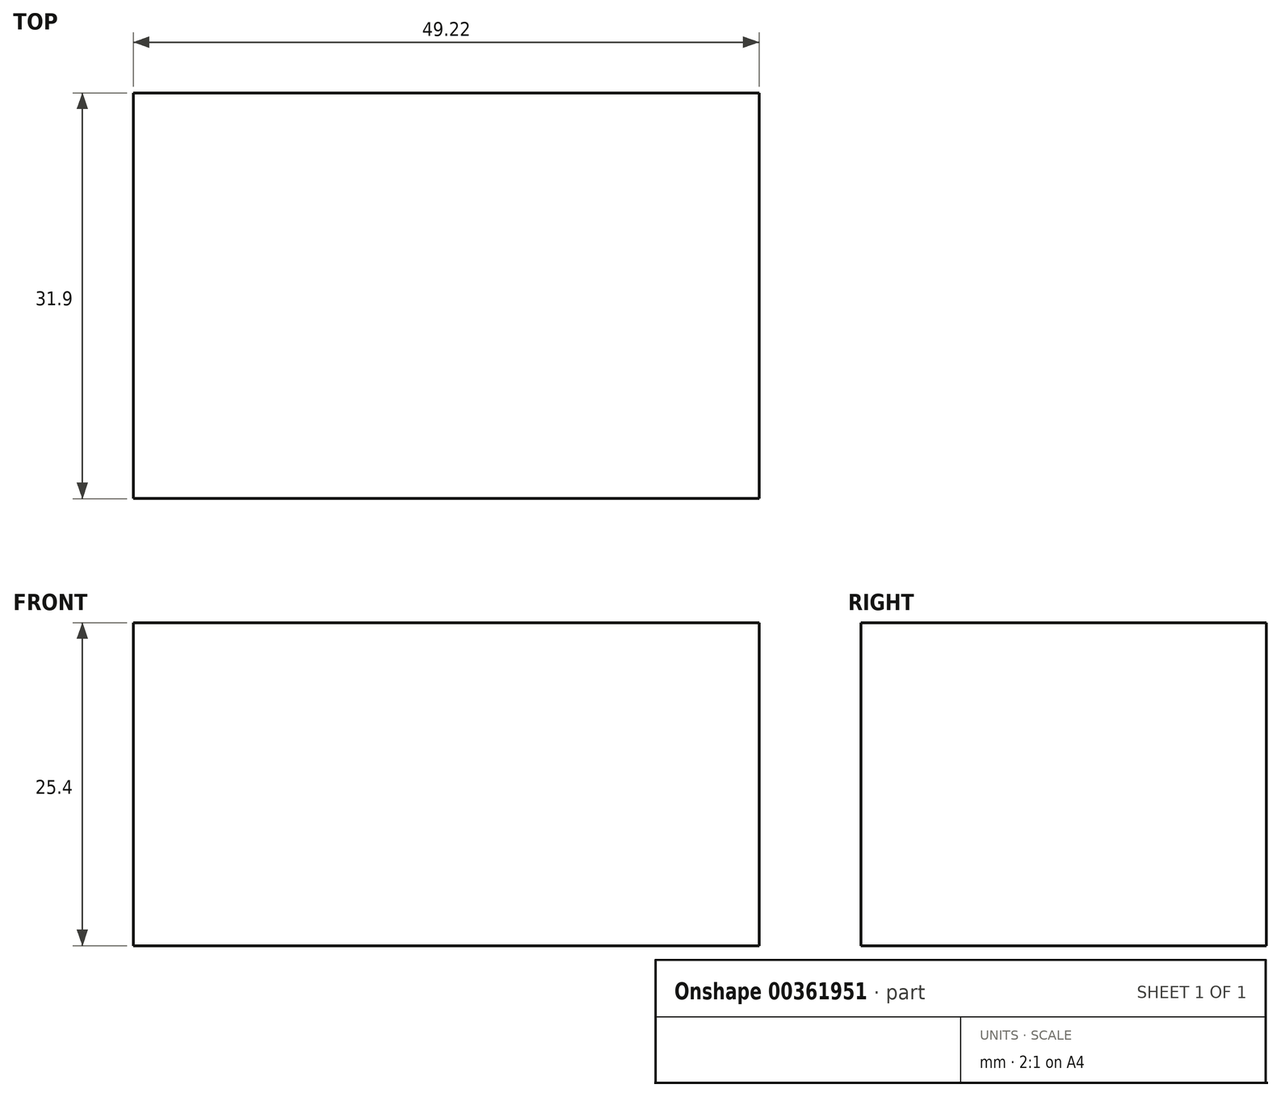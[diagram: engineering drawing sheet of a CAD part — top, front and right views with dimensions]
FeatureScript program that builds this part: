
annotation { "Feature Type Name" : "Feature", "Feature Type Description" : "" }
export const myFeature = defineFeature(function(context is Context, id is Id, definition is map)
    precondition{}
    {
        {
            var Q0;
            Q0=qCreatedBy(makeId("Top.planeOp"),FACE);
            var sketch = newSketch(context, id + "F0", { "sketchPlane" : qUnion([Q0])});
            skLineSegment(sketch, "E0.bottom", {"start": v(49.22, 0) * mm, "end": v(0, 0) * mm});
            skLineSegment(sketch, "E0.top", {"start": v(49.22, -31.9) * mm, "end": v(0, -31.9) * mm});
            skLineSegment(sketch, "E0.left", {"start": v(49.22, 0) * mm, "end": v(49.22, -31.9) * mm});
            skLineSegment(sketch, "E0.right", {"start": v(0, 0) * mm, "end": v(0, -31.9) * mm});
            skSolve(sketch);
        }
        {
            var Q0;
            Q0=makeQuery(id+"F0.imprint","IMPRINT",FACE,{"disambiguationData":[TD([[makeQuery(id+"F0.imprint","IMPRINT",EDGE,{"derivedFrom":sQuery(id+"F0.wireOp",EDGE,"E0.bottom")}),1.0]])]});
            var sketch = newSketch(context, id + "F1", { "sketchPlane" : qUnion([Q0])});
            skSolve(sketch);
        }
        {
            var Q0;
            Q0=makeQuery(id+"F1.imprint","IMPRINT",FACE,{"disambiguationData":[TD([[makeQuery(id+"F1.imprint","IMPRINT",EDGE,{"derivedFrom":makeQuery(id+"F0.imprint","IMPRINT",EDGE,{"derivedFrom":sQuery(id+"F0.wireOp",EDGE,"E0.bottom")})}),1.0]])]});
            extrude(context, id + "F2", {"entities" : qUnion([Q0]), "depth" : 25.4 * mm});
        }
    });
